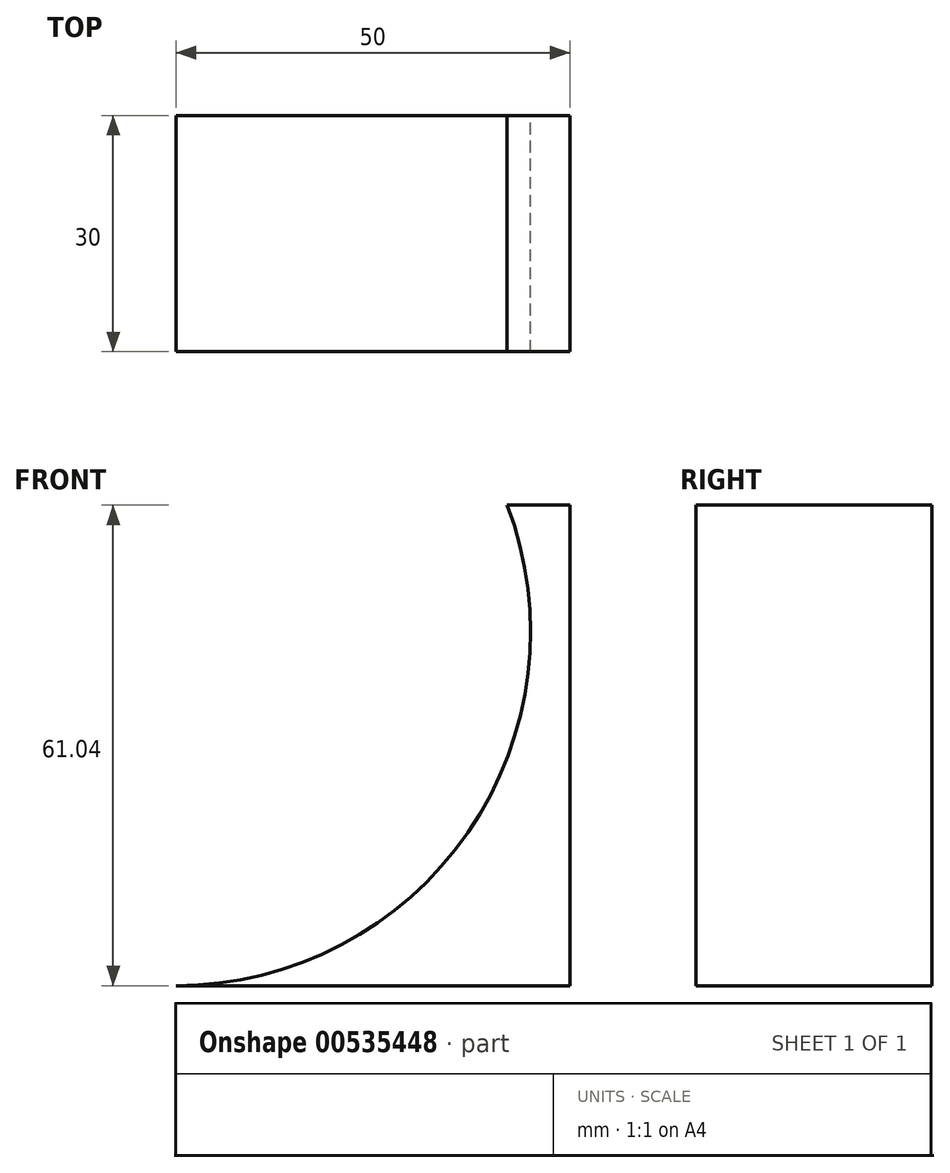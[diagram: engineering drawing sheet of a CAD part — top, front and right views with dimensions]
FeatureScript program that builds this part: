
annotation { "Feature Type Name" : "Feature", "Feature Type Description" : "" }
export const myFeature = defineFeature(function(context is Context, id is Id, definition is map)
    precondition{}
    {
        {
            var Q0;
            Q0=qCreatedBy(makeId("Front.planeOp"),FACE);
            var sketch = newSketch(context, id + "F0", { "sketchPlane" : qUnion([Q0])});
            skLineSegment(sketch, "E0.bottom", {"start": v(-25, -22.5) * mm, "end": v(25, -22.5) * mm});
            skLineSegment(sketch, "E0.top", {"start": v(-25, 22.5) * mm, "end": v(25, 22.5) * mm});
            skLineSegment(sketch, "E0.left", {"start": v(-25, -22.5) * mm, "end": v(-25, 22.5) * mm});
            skLineSegment(sketch, "E0.right", {"start": v(25, -22.5) * mm, "end": v(25, 22.5) * mm});
            skPoint(sketch, "E0.middle", {"position": v(0, 0) * mm});
            skCircle(sketch, "E1", {"center": v(-25, 22.5) * mm, "radius": 45 * mm});
            skLineSegment(sketch, "E2", {"start": v(17.04, 38.54) * mm, "end": v(25, 38.54) * mm});
            skLineSegment(sketch, "E3", {"start": v(25, 38.54) * mm, "end": v(25, 22.5) * mm});
            skSolve(sketch);
        }
        {
            var Q0;
            {var subQ0=sQuery(id+"F0.wireOp",EDGE,"E0.bottom");Q0=makeQuery(id+"F0.imprint","IMPRINT",FACE,{"disambiguationData":[TD([[makeQuery(id+"F0.imprint","IMPRINT",EDGE,{"derivedFrom":subQ0}),1.0]])]});}
            var Q1;
            {var subQ4=sQuery(id+"F0.wireOp",EDGE,"E2");Q1=makeQuery(id+"F0.imprint","IMPRINT",FACE,{"disambiguationData":[TD([[makeQuery(id+"F0.imprint","IMPRINT",EDGE,{"derivedFrom":subQ4}),-1.0]])]});}
            extrude(context, id + "F1", {"entities" : qUnion([Q0, Q1]), "depth" : 30 * mm, "offsetDistance" : 25 * mm});
        }
    });
